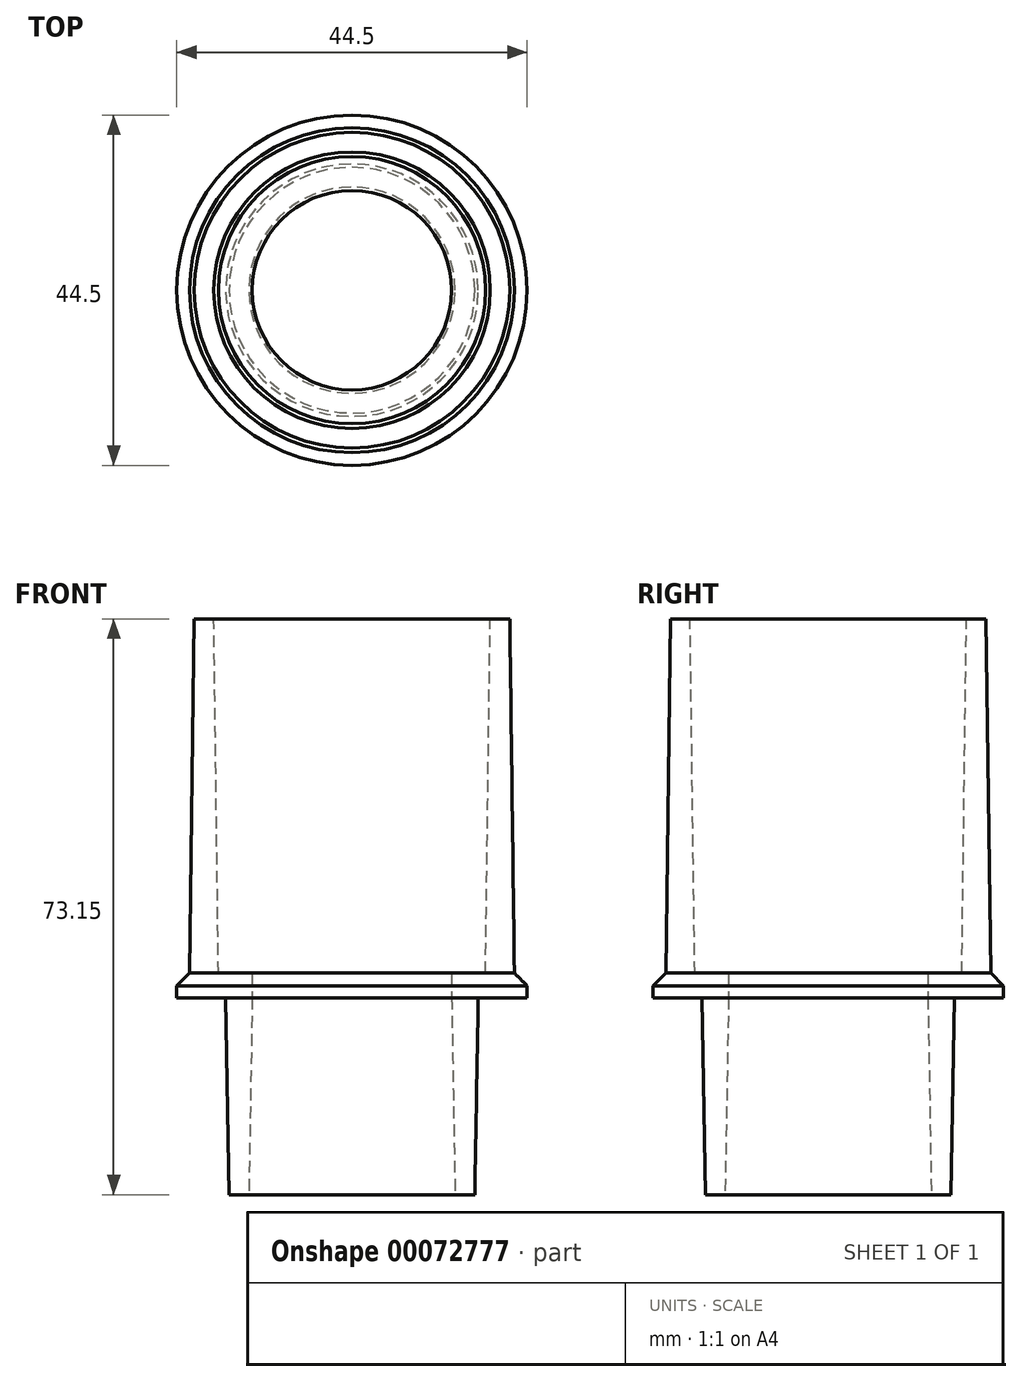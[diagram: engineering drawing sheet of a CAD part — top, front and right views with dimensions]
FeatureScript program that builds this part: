
annotation { "Feature Type Name" : "Feature", "Feature Type Description" : "" }
export const myFeature = defineFeature(function(context is Context, id is Id, definition is map)
    precondition{}
    {
        {
            var Q0;
            Q0=qCreatedBy(makeId("Top.planeOp"),FACE);
            var sketch = newSketch(context, id + "F0", { "sketchPlane" : qUnion([Q0])});
            skCircle(sketch, "E0", {"center": v(0, 0) * mm, "radius": 13.1 * mm});
            skCircle(sketch, "E1", {"center": v(0, 0) * mm, "radius": 15.6 * mm});
            skSolve(sketch);
        }
        {
            var Q0;
            Q0=makeQuery(id+"F0.imprint","IMPRINT",FACE,{"disambiguationData":[TD([[makeQuery(id+"F0.imprint","IMPRINT",EDGE,{"derivedFrom":sQuery(id+"F0.wireOp",EDGE,"E0")}),-1.0]])]});
            extrude(context, id + "F1", {"entities" : qUnion([Q0]), "depth" : 25 * mm, "hasDraft" : true, "draftAngle" : 1 * degree});
        }
        {
            var Q0;
            Q0=makeQuery(id+"F1.opExtrude","CAP_FACE",FACE,{"disambiguationData":[OSD([sQuery(id+"F0.wireOp",EDGE,"E0"),sQuery(id+"F0.wireOp",EDGE,"E1")])],"isStart":false});
            var sketch = newSketch(context, id + "F2", { "sketchPlane" : qUnion([Q0])});
            skCircle(sketch, "E2", {"center": v(0, 0) * mm, "radius": 12.66 * mm});
            skCircle(sketch, "E3", {"center": v(0, 0) * mm, "radius": 22.25 * mm});
            skSolve(sketch);
        }
        {
            var Q0;
            Q0 = qSketchRegion(id + "F2", true);
            extrude(context, id + "F3", {"entities" : qUnion([Q0]), "operationType" : NewBodyOperationType.ADD, "depth" : 3.15 * mm});
        }
        {
            var Q0;
            Q0=makeQuery(id+"F3.opExtrude","CAP_FACE",FACE,{"disambiguationData":[OSD([sQuery(id+"F2.wireOp",EDGE,"E2"),sQuery(id+"F2.wireOp",EDGE,"E3")])],"isStart":false});
            cPlane(context, id + "F4", {"entities" : qUnion([Q0]), "cplaneType" : CPlaneType.OFFSET, "offset" : 45 * mm, "width" : 150 * mm, "height" : 150 * mm});
        }
        {
            var Q0;
            Q0=qCreatedBy(id+"F4.planeOp",FACE);
            var sketch = newSketch(context, id + "F5", { "sketchPlane" : qUnion([Q0])});
            skCircle(sketch, "E4", {"center": v(0, 0) * mm, "radius": 17.55 * mm});
            skCircle(sketch, "E5", {"center": v(0, 0) * mm, "radius": 20.05 * mm});
            skSolve(sketch);
        }
        {
            var Q0;
            Q0=makeQuery(id+"F5.imprint","IMPRINT",FACE,{"disambiguationData":[TD([[makeQuery(id+"F5.imprint","IMPRINT",EDGE,{"derivedFrom":sQuery(id+"F5.wireOp",EDGE,"E4")}),-1.0]])]});
            var Q1;
            Q1=makeQuery(id+"F3.opExtrude","CAP_FACE",FACE,{"disambiguationData":[OSD([sQuery(id+"F2.wireOp",EDGE,"E2"),sQuery(id+"F2.wireOp",EDGE,"E3")])],"isStart":false});
            extrude(context, id + "F6", {"entities" : qUnion([Q0]), "operationType" : NewBodyOperationType.ADD, "endBound" : BoundingType.UP_TO_SURFACE, "oppositeDirection" : true, "endBoundEntityFace" : qUnion([Q1]), "depth" : 25 * mm, "hasDraft" : true, "draftAngle" : .75 * degree});
        }
        {
            var Q0;
            Q0=makeQuery(id+"F3.opExtrude","CAP_EDGE",EDGE,{"disambiguationData":[OSD([sQuery(id+"F2.wireOp",EDGE,"E3")])],"isStart":false});
            chamfer(context, id + "F7", {"entities" : qUnion([Q0]), "width" : 1.61 * mm, "tangentPropagation" : true});
        }
    });
